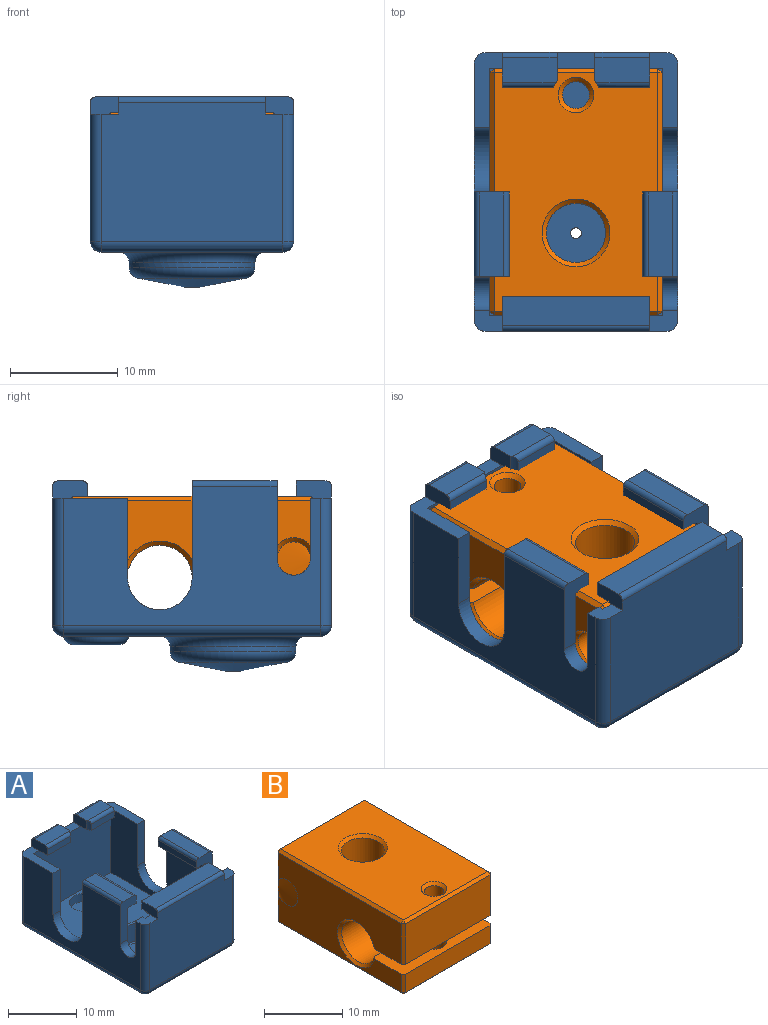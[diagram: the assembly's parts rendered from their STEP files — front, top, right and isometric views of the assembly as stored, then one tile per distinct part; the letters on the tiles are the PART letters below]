
ASSEMBLY  parts=2 mates=1
PART A: 107 faces, bbox 18.9x25.9x17.7 mm
  f0: plane 6.97x2.6mm, normal (0,0,1), area 11.6mm2, adj f1,f7,f17,f26,f40,f49,f95
  f1: plane 23.92x12.94mm, normal (1,0,0), area 212.2mm2, adj f0,f13,f26,f32,f35,f37,f39,f92
  f2: plane 23.92x12.94mm, normal (-1,0,0), area 212.2mm2, adj f6,f14,f24,f28,f29,f36,f42,f88
  f3: plane 3.25x1.6mm, normal (-1,0,0), area 5mm2, adj f4,f14,f16,f18,f44,f96,f97,f105
  f4: plane 13.71x1.45mm, normal (0,1,0), area 19.9mm2, adj f3,f5,f18,f96
  f5: plane 3.25x1.6mm, normal (1,0,0), area 5mm2, adj f4,f13,f16,f18,f44,f96,f97,f105
  f6: plane 6.97x2.6mm, normal (0,0,1), area 11.6mm2, adj f2,f8,f17,f24,f41,f49,f91
  f7: plane 23.02x11.54mm, normal (-1,0,0), area 183.3mm2, adj f0,f13,f37,f39,f45,f48,f49,f51
  f8: plane 23.02x11.54mm, normal (1,0,0), area 183.3mm2, adj f6,f14,f36,f42,f47,f48,f49,f53
  f9: plane 4.75x1.1mm, normal (0,-1,0), area 5.2mm2, adj f40,f71,f79,f100
  f10: plane 2.64x1.6mm, normal (-1,0,0), area 4.2mm2, adj f15,f17,f22,f71,f79,f104
  f11: plane 2.64x1.6mm, normal (1,0,0), area 4.2mm2, adj f15,f17,f20,f46,f82,f98
  f12: plane 4.75x1.1mm, normal (0,-1,0), area 5.2mm2, adj f41,f46,f82,f101
  f13: plane 2.6x1.95mm, normal (0,0,1), area 4.3mm2, adj f1,f5,f7,f16,f35,f48,f93
  f14: plane 2.6x1.95mm, normal (0,0,1), area 4.3mm2, adj f2,f3,f8,f16,f29,f48,f89
  f15: plane 3.51x1.45mm, normal (0,0,1), area 5.1mm2, adj f10,f11,f17,f49
  f16: plane 16.91x12.94mm, normal (0,-1,0), area 215.3mm2, adj f3,f5,f13,f14,f29,f33,f35,f105
  f17: plane 16.91x12.94mm, normal (0,1,0), area 211.4mm2, adj f0,f6,f10,f11,f15,f24,f26,f27
  f18: plane 13.71x2.75mm, normal (0,0,1), area 37.7mm2, adj f3,f4,f5,f105
  f19: plane 7.9x2.25mm, normal (0,0,1), area 17.8mm2, adj f37,f39,f99,f106
  f20: plane 5.1x2.25mm, normal (0,0,1), area 11.5mm2, adj f11,f41,f82,f98,f101
  f21: plane 7.9x2.25mm, normal (0,0,1), area 17.8mm2, adj f36,f42,f102,f103
  f22: plane 5.1x2.25mm, normal (0,0,1), area 11.5mm2, adj f10,f40,f79,f100,f104
  f23: plane 23.92x16.91mm, normal (0,0,-1), area 227.9mm2, adj f27,f28,f32,f33,f73,f78
  f24: cylinder r=1mm len=11.84mm, axis (0,0,-1), area 18.6mm2, adj f2,f6,f17,f25
  f25: sphere r=1mm, area 1.6mm2, adj f24,f27,f28
  f26: cylinder r=1mm len=11.84mm, axis (0,0,1), area 18.6mm2, adj f0,f1,f17,f30
  f27: cylinder r=1mm len=16.91mm, axis (-1,0,0), area 26.6mm2, adj f17,f23,f25,f30
  f28: cylinder r=1mm len=23.92mm, axis (0,-1,0), area 37.6mm2, adj f2,f23,f25,f31
  f29: cylinder r=1mm len=11.84mm, axis (0,0,1), area 18.6mm2, adj f2,f14,f16,f31
  f30: sphere r=1mm, area 1.6mm2, adj f26,f27,f32
  f31: sphere r=1mm, area 1.6mm2, adj f28,f29,f33
  f32: cylinder r=1mm len=23.92mm, axis (0,1,0), area 37.6mm2, adj f1,f23,f30,f34
  f33: cylinder r=1mm len=16.91mm, axis (1,0,0), area 26.6mm2, adj f16,f23,f31,f34
  f34: sphere r=1mm, area 1.6mm2, adj f32,f33,f35
  f35: cylinder r=1mm len=11.84mm, axis (0,0,-1), area 18.6mm2, adj f1,f13,f16,f34
  f36: plane 7.22x3.25mm, normal (0,-1,0), area 13.2mm2, adj f2,f8,f21,f43,f47,f88,f102,f103
  f37: plane 7.22x3.25mm, normal (0,-1,0), area 13.2mm2, adj f1,f7,f19,f38,f45,f92,f99,f106
  f38: plane 7.9x1.1mm, normal (-1,0,0), area 8.7mm2, adj f37,f39,f45,f99
  f39: plane 8.99x3.25mm, normal (0,1,0), area 15.8mm2, adj f1,f7,f19,f38,f45,f94,f99,f106
  f40: plane 3.25x1.6mm, normal (1,0,0), area 5.1mm2, adj f0,f9,f17,f22,f71,f100,f104
  f41: plane 3.25x1.6mm, normal (-1,0,0), area 5.1mm2, adj f6,f12,f17,f20,f46,f98,f101
  f42: plane 8.99x3.25mm, normal (0,1,0), area 15.8mm2, adj f2,f8,f21,f43,f47,f90,f102,f103
  f43: plane 7.9x1.1mm, normal (1,0,0), area 8.7mm2, adj f36,f42,f47,f102
  f44: plane 13.71x0.5mm, normal (0,0,-1), area 3.1mm2, adj f3,f5,f48,f57,f58,f59,f97
  f45: plane 7.9x1.8mm, normal (0,0,-1), area 12.5mm2, adj f7,f37,f38,f39,f60,f61,f62
  f46: plane 5.1x1.8mm, normal (0,0,-1), area 8.3mm2, adj f11,f12,f41,f49,f66,f67,f68,f82
  f47: plane 7.9x1.8mm, normal (0,0,-1), area 12.5mm2, adj f8,f36,f42,f43,f56,f69,f70
  f48: plane 16.01x11.54mm, normal (0,1,0), area 184mm2, adj f7,f8,f13,f14,f44,f50,f55,f57
  f49: plane 16.01x11.54mm, normal (0,-1,0), area 183mm2, adj f0,f6,f7,f8,f15,f46,f52,f54
  f50: plane 10.81x0.35mm, normal (0,0,-1), area 3.8mm2, adj f48,f57,f58,f59
  f51: plane 5x0.35mm, normal (0,0,-1), area 1.7mm2, adj f7,f60,f61,f62
  f52: plane 2.2x0.35mm, normal (0,0,-1), area 0.8mm2, adj f49,f66,f67,f68
  f53: plane 5x0.35mm, normal (0,0,-1), area 1.8mm2, adj f8,f56,f69,f70
  f54: plane 2.2x0.35mm, normal (0,0,-1), area 0.8mm2, adj f49,f63,f64,f65
  f55: plane 23.02x16.01mm, normal (0,0,1), area 289mm2, adj f7,f8,f48,f49,f81,f86
  f56: plane 0.35x0.15mm, normal (0,1,0), area 0.1mm2, adj f8,f47,f53,f70
  f57: plane 0.35x0.15mm, normal (1,0,0), area 0.1mm2, adj f44,f48,f50,f58
  f58: plane 10.81x0.15mm, normal (0,-1,0), area 1.6mm2, adj f44,f50,f57,f59
  f59: plane 0.35x0.15mm, normal (-1,0,0), area 0.1mm2, adj f44,f48,f50,f58
  f60: plane 0.35x0.15mm, normal (0,1,0), area 0.1mm2, adj f7,f45,f51,f61
  f61: plane 5x0.15mm, normal (1,0,0), area 0.7mm2, adj f45,f51,f60,f62
  f62: plane 0.35x0.15mm, normal (0,-1,0), area 0.1mm2, adj f7,f45,f51,f61
  f63: plane 0.35x0.15mm, normal (-1,0,0), area 0.1mm2, adj f49,f54,f64,f71
  f64: plane 2.2x0.15mm, normal (0,1,0), area 0.3mm2, adj f54,f63,f65,f71
  f65: plane 0.35x0.15mm, normal (1,0,0), area 0.1mm2, adj f49,f54,f64,f71
  f66: plane 0.35x0.15mm, normal (-1,0,0), area 0.1mm2, adj f46,f49,f52,f67
  f67: plane 2.2x0.15mm, normal (0,1,0), area 0.3mm2, adj f46,f52,f66,f68
  f68: plane 0.35x0.15mm, normal (1,0,0), area 0.1mm2, adj f46,f49,f52,f67
  f69: plane 0.35x0.15mm, normal (0,-1,0), area 0.1mm2, adj f8,f47,f53,f70
  f70: plane 5x0.15mm, normal (-1,0,0), area 0.7mm2, adj f47,f53,f56,f69
  f71: plane 5.1x1.8mm, normal (0,0,-1), area 8.3mm2, adj f9,f10,f40,f49,f63,f64,f65,f79
  f72: plane 4.14x4.14mm, normal (0,0,-1), area 13.5mm2, adj f73
  f73: torus R=2.07mm, axis (0,0,-1), area 22.8mm2, adj f23,f72
  f74: cylinder r=5.85mm len=11.7mm, axis (0,0,1), area 15.6mm2, adj f77,f78
  f75: plane 1.41x1.41mm, normal (0,0,-1), area 0.8mm2, adj f76,f85
  f76: cone r=5.85mm half-angle=79deg, axis (0,0,1), area 79.7mm2, adj f75,f77
  f77: torus R=4.85mm, axis (0,0,-1), area 48.2mm2, adj f74,f76
  f78: torus R=6.85mm, axis (0,0,1), area 61.3mm2, adj f23,f74
  f79: cylinder r=2.25mm len=1.6mm, axis (0,0,-1), area 1.1mm2, adj f9,f10,f22,f71,f100
  f80: plane 4.5x4.5mm, normal (0,0,1), area 15.9mm2, adj f81
  f81: cylinder r=2.25mm len=4.5mm, axis (0,0,-1), area 20.5mm2, adj f55,f80
  f82: cylinder r=2.25mm len=1.6mm, axis (0,0,-1), area 1.1mm2, adj f11,f12,f20,f46,f101
  f83: cylinder r=4.3mm len=8.6mm, axis (0,0,1), area 85.1mm2, adj f86,f87
  f84: plane 8.2x8.2mm, normal (0,0,1), area 52mm2, adj f85,f87
  f85: cylinder r=0.5mm len=1.15mm, axis (0,0,1), area 3.6mm2, adj f75,f84
  f86: torus R=4.5mm, axis (0,0,1), area 8.6mm2, adj f55,f83
  f87: torus R=4.1mm, axis (0,0,1), area 8.3mm2, adj f83,f84
  f88: cylinder r=1.55mm len=3.1mm, axis (1,0,0), area 7.1mm2, adj f2,f8,f36,f89
  f89: plane 5.62x1.45mm, normal (0,1,0), area 8.1mm2, adj f2,f8,f14,f88
  f90: cylinder r=3mm len=6mm, axis (1,0,0), area 13.7mm2, adj f2,f8,f42,f91
  f91: plane 7.39x1.45mm, normal (0,-1,0), area 10.7mm2, adj f2,f6,f8,f90
  f92: cylinder r=1.55mm len=3.1mm, axis (1,0,0), area 7.1mm2, adj f1,f7,f37,f93
  f93: plane 5.62x1.45mm, normal (0,1,0), area 8.1mm2, adj f1,f7,f13,f92
  f94: cylinder r=3mm len=6mm, axis (1,0,0), area 13.7mm2, adj f1,f7,f39,f95
  f95: plane 7.39x1.45mm, normal (0,-1,0), area 10.7mm2, adj f0,f1,f7,f94
  f96: plane 13.71x0.94mm, normal (0,0,-1), area 12.9mm2, adj f3,f4,f5,f97
  f97: cylinder r=0.5mm len=13.71mm, axis (-1,0,0), area 5.5mm2, adj f3,f5,f44,f96
  f98: cylinder r=0.5mm len=5.1mm, axis (1,0,0), area 4mm2, adj f11,f17,f20,f41
  f99: cylinder r=0.5mm len=7.9mm, axis (0,-1,0), area 6.2mm2, adj f19,f37,f38,f39
  f100: cylinder r=0.5mm len=5.02mm, axis (1,0,0), area 3.8mm2, adj f9,f22,f40,f79
  f101: cylinder r=0.5mm len=5.02mm, axis (1,0,0), area 3.8mm2, adj f12,f20,f41,f82
  f102: cylinder r=0.5mm len=7.9mm, axis (0,1,0), area 6.2mm2, adj f21,f36,f42,f43
  f103: cylinder r=0.5mm len=7.9mm, axis (0,1,0), area 6.2mm2, adj f2,f21,f36,f42
  f104: cylinder r=0.5mm len=5.1mm, axis (1,0,0), area 4mm2, adj f10,f17,f22,f40
  f105: cylinder r=0.5mm len=13.71mm, axis (-1,0,0), area 10.8mm2, adj f3,f5,f16,f18
  f106: cylinder r=0.5mm len=7.9mm, axis (0,-1,0), area 6.2mm2, adj f1,f19,f37,f39
PART B: 46 faces, bbox 16x23x11.5 mm
  f0: cylinder r=1.55mm len=15.21mm, axis (-1,0,0), area 142.7mm2, adj f14,f22,f26
  f1: plane 16.02x5.64mm, normal (0,0,-1), area 84.9mm2, adj f2,f8,f9,f10,f12,f15,f17,f39
  f2: cylinder r=3mm len=15.21mm, axis (-1,0,0), area 262.9mm2, adj f1,f3,f39,f40
  f3: plane 16.02x5.62mm, normal (0,0,1), area 81.5mm2, adj f2,f4,f9,f10,f13,f32,f38,f39
  f4: plane 15.21x2.85mm, normal (0,-1,0), area 43.3mm2, adj f3,f32,f36,f38
  f5: plane 22.22x15.21mm, normal (0,0,-1), area 285.7mm2, adj f30,f31,f35,f36,f43,f44,f45
  f6: plane 15.21x10.74mm, normal (0,1,0), area 163.4mm2, adj f24,f25,f29,f30
  f7: plane 22.22x15.21mm, normal (0,0,1), area 298.2mm2, adj f18,f19,f23,f24,f41,f42
  f8: plane 15.21x6.34mm, normal (0,-1,0), area 96.4mm2, adj f1,f15,f17,f18
  f9: plane 22.22x10.74mm, normal (1,0,0), area 183.4mm2, adj f1,f3,f17,f23,f26,f29,f35,f38
  f10: plane 22.22x10.74mm, normal (-1,0,0), area 183.4mm2, adj f1,f3,f15,f19,f22,f25,f31,f32
  f11: cylinder r=2.75mm len=10.74mm, axis (0,0,-1), area 185.6mm2, adj f42,f45
  f12: cylinder r=1.25mm len=6.34mm, axis (0,0,-1), area 49.8mm2, adj f1,f41
  f13: cylinder r=1.6mm len=3.2mm, axis (0,0,-1), area 28.7mm2, adj f3,f44
  f14: cylinder r=1.25mm len=4.45mm, axis (0,0,-1), area 32.3mm2, adj f0,f43
  f15: plane 6.34x0.4mm, normal (-0.71,-0.71,0), area 3.6mm2, adj f1,f8,f10,f16
  f16: plane 0.4x0.4mm, normal (-0.58,-0.58,0.58), area 0.1mm2, adj f15,f18,f19
  f17: plane 6.34x0.4mm, normal (0.71,-0.71,0), area 3.6mm2, adj f1,f8,f9,f20
  f18: plane 15.21x0.4mm, normal (0,-0.71,0.71), area 8.6mm2, adj f7,f8,f16,f20
  f19: plane 22.22x0.4mm, normal (-0.71,0,0.71), area 12.6mm2, adj f7,f10,f16,f21
  f20: plane 0.4x0.4mm, normal (0.58,-0.58,0.58), area 0.1mm2, adj f17,f18,f23
  f21: plane 0.4x0.4mm, normal (-0.58,0.58,0.58), area 0.1mm2, adj f19,f24,f25
  f22: cone r=1.95mm half-angle=45deg, axis (-1,0,0), area 5.9mm2, adj f0,f10,f25
  f23: plane 22.22x0.4mm, normal (0.71,0,0.71), area 12.6mm2, adj f7,f9,f20,f27
  f24: plane 15.21x0.4mm, normal (0,0.71,0.71), area 8.6mm2, adj f6,f7,f21,f27
  f25: plane 10.74x0.4mm, normal (-0.71,0.71,0), area 5.8mm2, adj f6,f10,f21,f22,f28
  f26: cone r=1.55mm half-angle=45deg, axis (1,0,0), area 5.9mm2, adj f0,f9,f29
  f27: plane 0.4x0.4mm, normal (0.58,0.58,0.58), area 0.1mm2, adj f23,f24,f29
  f28: plane 0.4x0.4mm, normal (-0.58,0.58,-0.58), area 0.1mm2, adj f25,f30,f31
  f29: plane 10.74x0.4mm, normal (0.71,0.71,0), area 5.8mm2, adj f6,f9,f26,f27,f33
  f30: plane 15.21x0.4mm, normal (0,0.71,-0.71), area 8.6mm2, adj f5,f6,f28,f33
  f31: plane 22.22x0.4mm, normal (-0.71,0,-0.71), area 12.6mm2, adj f5,f10,f28,f34
  f32: plane 2.85x0.4mm, normal (-0.71,-0.71,0), area 1.6mm2, adj f3,f4,f10,f34
  f33: plane 0.4x0.4mm, normal (0.58,0.58,-0.58), area 0.1mm2, adj f29,f30,f35
  f34: plane 0.4x0.4mm, normal (-0.58,-0.58,-0.58), area 0.1mm2, adj f31,f32,f36
  f35: plane 22.22x0.4mm, normal (0.71,0,-0.71), area 12.6mm2, adj f5,f9,f33,f37
  f36: plane 15.21x0.4mm, normal (0,-0.71,-0.71), area 8.6mm2, adj f4,f5,f34,f37
  f37: plane 0.4x0.4mm, normal (0.58,-0.58,-0.58), area 0.1mm2, adj f35,f36,f38
  f38: plane 2.85x0.4mm, normal (0.71,-0.71,0), area 1.6mm2, adj f3,f4,f9,f37
  f39: cone r=3mm half-angle=45deg, axis (1,0,0), area 10.5mm2, adj f1,f2,f3,f9
  f40: cone r=3.4mm half-angle=45deg, axis (-1,0,0), area 10.5mm2, adj f1,f2,f3,f10
  f41: cone r=1.25mm half-angle=45deg, axis (0,0,1), area 5.2mm2, adj f7,f12
  f42: cone r=2.75mm half-angle=45deg, axis (0,0,1), area 10.5mm2, adj f7,f11
  f43: cone r=1.25mm half-angle=45deg, axis (0,0,-1), area 5.2mm2, adj f5,f14
  f44: cone r=1.6mm half-angle=45deg, axis (0,0,-1), area 6.4mm2, adj f5,f13
  f45: cone r=2.75mm half-angle=45deg, axis (0,0,-1), area 10.5mm2, adj f5,f11
PLACE A t=(17.88,2.91,-4.72)mm
PLACE B rot(axis=(0,0,-1),180deg) t=(17.88,2.91,2.5)mm
MATE fastened A.f74 <-> B.f11  axis (0,0,1) through (17.88,-0.9,-3.27)mm
